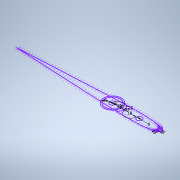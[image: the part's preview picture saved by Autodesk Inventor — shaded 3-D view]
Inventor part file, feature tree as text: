
AUTODESK INVENTOR PART (.ipt)
format: ipt  version: 2022 (Build 260153000, 153)  size: 135,680 bytes
history: native  units: mm
features: sketch x1
ambient origin geometry x8: Origin, YZ Plane, XZ Plane, XY Plane, X Axis, Y Axis, Z Axis, Center Point
feature tree (1):
  sketch  "Sketch1"  dims[d0=23.0mm d1=27.0mm d2=8.0mm d3=5.0mm d4=5.0mm d5=18.0mm d6=18.0mm d7=8.0mm]
